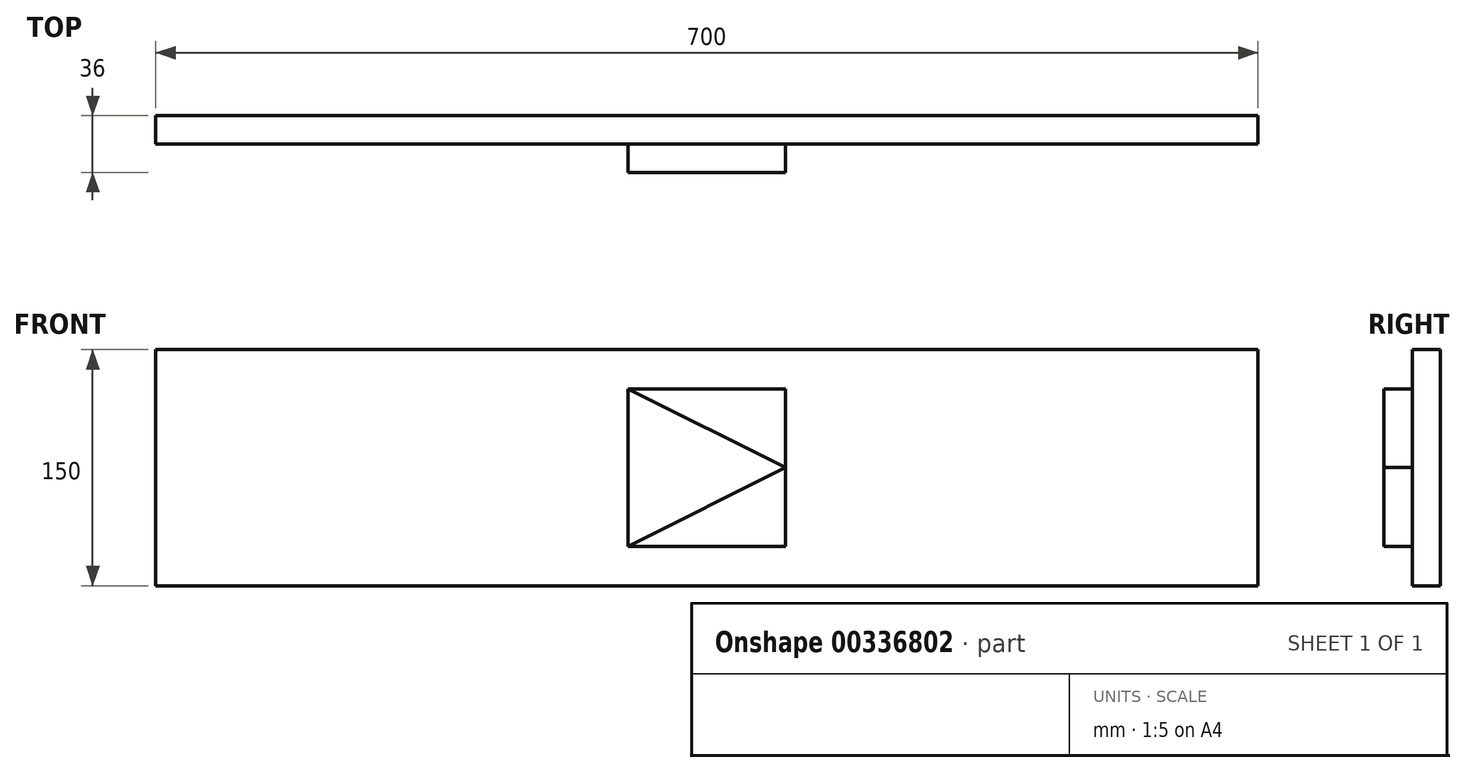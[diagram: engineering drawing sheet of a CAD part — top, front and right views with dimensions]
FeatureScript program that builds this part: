
annotation { "Feature Type Name" : "Feature", "Feature Type Description" : "" }
export const myFeature = defineFeature(function(context is Context, id is Id, definition is map)
    precondition{}
    {
        {
            var Q0;
            Q0=qCreatedBy(makeId("Front.planeOp"),FACE);
            var sketch = newSketch(context, id + "F0", { "sketchPlane" : qUnion([Q0])});
            skLineSegment(sketch, "E0.bottom", {"start": v(-350, 75) * mm, "end": v(350, 75) * mm});
            skLineSegment(sketch, "E0.top", {"start": v(-350, -75) * mm, "end": v(350, -75) * mm});
            skLineSegment(sketch, "E0.left", {"start": v(-350, 75) * mm, "end": v(-350, -75) * mm});
            skLineSegment(sketch, "E0.right", {"start": v(350, 75) * mm, "end": v(350, -75) * mm});
            skPoint(sketch, "E0.middle", {"position": v(0, 0) * mm});
            skSolve(sketch);
        }
        {
            var Q0;
            Q0 = qSketchRegion(id + "F0", true);
            extrude(context, id + "F1", {"entities" : qUnion([Q0]), "depth" : 18 * mm});
        }
        {
            var Q0;
            Q0=makeQuery(id+"F1.opExtrude","CAP_FACE",FACE,{"disambiguationData":[OSD([sQuery(id+"F0.wireOp",EDGE,"E0.bottom"),sQuery(id+"F0.wireOp",EDGE,"E0.top"),sQuery(id+"F0.wireOp",EDGE,"E0.left"),sQuery(id+"F0.wireOp",EDGE,"E0.right")])],"isStart":false});
            var sketch = newSketch(context, id + "F2", { "sketchPlane" : qUnion([Q0])});
            skLineSegment(sketch, "E1.bottom", {"start": v(-50, 50) * mm, "end": v(50, 50) * mm});
            skLineSegment(sketch, "E1.top", {"start": v(-50, -50) * mm, "end": v(50, -50) * mm});
            skLineSegment(sketch, "E1.left", {"start": v(-50, 50) * mm, "end": v(-50, -50) * mm});
            skLineSegment(sketch, "E1.right", {"start": v(50, 50) * mm, "end": v(50, -50) * mm});
            skPoint(sketch, "E1.middle", {"position": v(0, 0) * mm});
            skSolve(sketch);
        }
        {
            var Q0;
            Q0 = qSketchRegion(id + "F2", true);
            extrude(context, id + "F3", {"entities" : qUnion([Q0]), "depth" : 18 * mm});
        }
        {
            var Q0;
            Q0=makeQuery(id+"F1.opExtrude","CAP_FACE",FACE,{"disambiguationData":[OSD([sQuery(id+"F0.wireOp",EDGE,"E0.bottom"),sQuery(id+"F0.wireOp",EDGE,"E0.top"),sQuery(id+"F0.wireOp",EDGE,"E0.left"),sQuery(id+"F0.wireOp",EDGE,"E0.right")])],"isStart":false});
            var sketch = newSketch(context, id + "F4", { "sketchPlane" : qUnion([Q0])});
            skLineSegment(sketch, "E2.bottom", {"start": v(-50, 50) * mm, "end": v(50, 50) * mm, "construction": true});
            skLineSegment(sketch, "E2.top", {"start": v(-50, -50) * mm, "end": v(50, -50) * mm, "construction": true});
            skLineSegment(sketch, "E2.left", {"start": v(-50, 50) * mm, "end": v(-50, -50) * mm, "construction": true});
            skLineSegment(sketch, "E2.right", {"start": v(50, 50) * mm, "end": v(50, -50) * mm, "construction": true});
            skPoint(sketch, "E2.middle", {"position": v(0, 0) * mm});
            skLineSegment(sketch, "E3", {"start": v(-50, 50) * mm, "end": v(50, 0) * mm});
            skLineSegment(sketch, "E4", {"start": v(50, 0) * mm, "end": v(-50, -50) * mm});
            skLineSegment(sketch, "E5", {"start": v(-50, 50) * mm, "end": v(-50, -50) * mm});
            skSolve(sketch);
        }
        {
            var Q0;
            Q0 = qSketchRegion(id + "F4", true);
            extrude(context, id + "F5", {"entities" : qUnion([Q0]), "depth" : 18 * mm});
        }
    });
